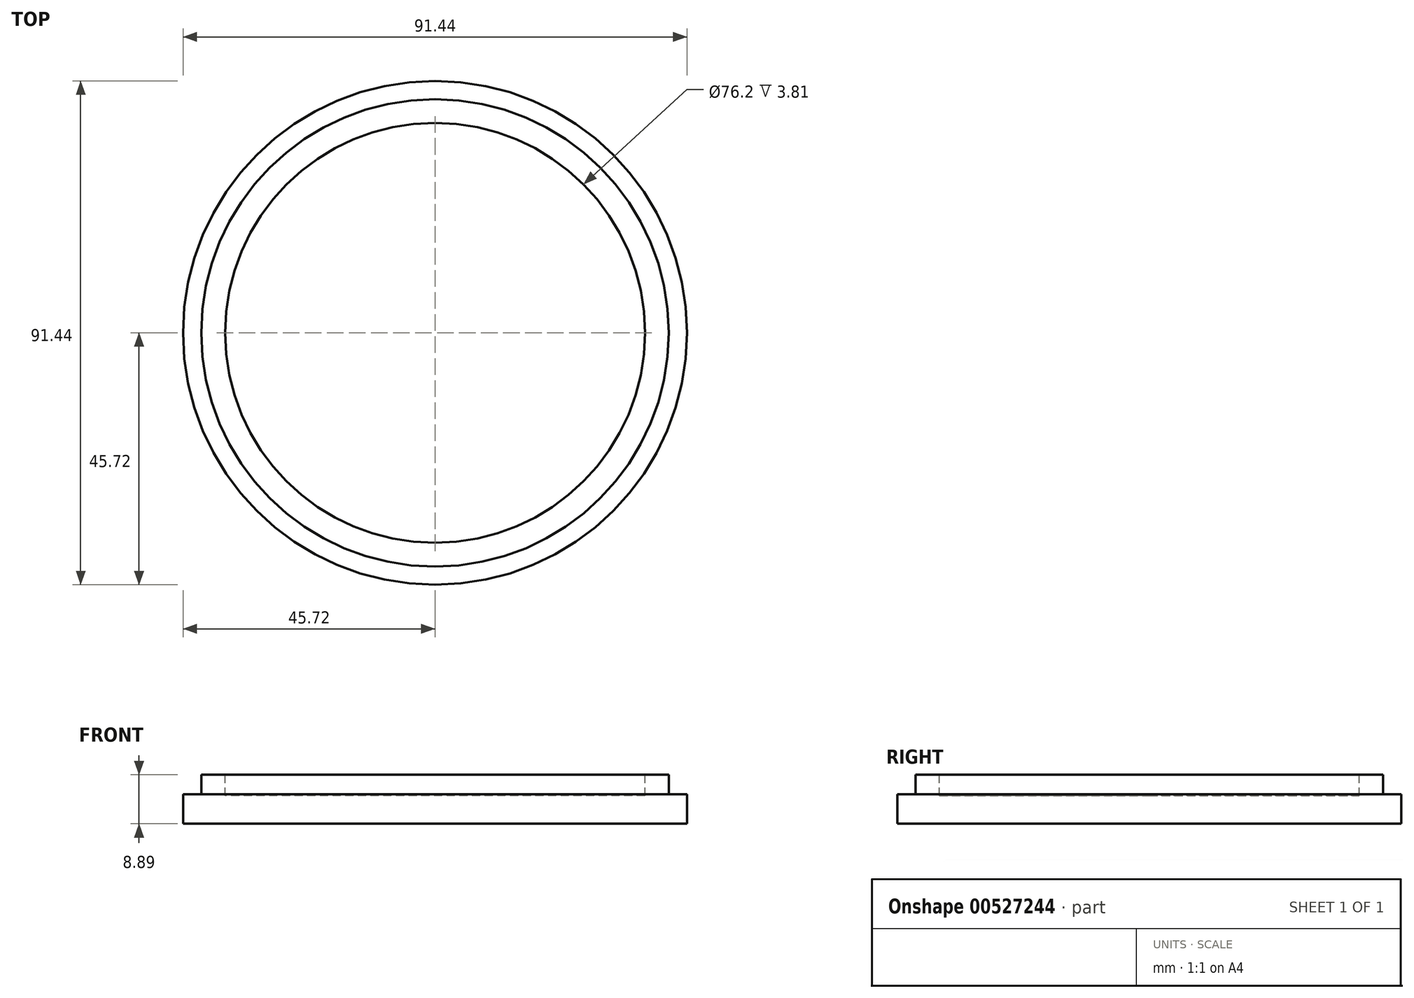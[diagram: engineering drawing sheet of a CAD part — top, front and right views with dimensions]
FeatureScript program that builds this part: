
annotation { "Feature Type Name" : "Feature", "Feature Type Description" : "" }
export const myFeature = defineFeature(function(context is Context, id is Id, definition is map)
    precondition{}
    {
        {
            var Q0;
            Q0=qCreatedBy(makeId("Top.planeOp"),FACE);
            var sketch = newSketch(context, id + "F0", { "sketchPlane" : qUnion([Q0])});
            skCircle(sketch, "E0", {"center": v(0, 0) * mm, "radius": 45.72 * mm});
            skSolve(sketch);
        }
        {
            var Q0;
            Q0 = qSketchRegion(id + "F0", true);
            extrude(context, id + "F1", {"entities" : qUnion([Q0]), "depth" : 5.33 * mm, "offsetDistance" : 25.4 * mm});
        }
        {
            var Q0;
            Q0=qCreatedBy(makeId("Top.planeOp"),FACE);
            var sketch = newSketch(context, id + "F2", { "sketchPlane" : qUnion([Q0])});
            skCircle(sketch, "E1", {"center": v(0, 0) * mm, "radius": 42.42 * mm});
            skSolve(sketch);
        }
        {
            var Q0;
            Q0 = qSketchRegion(id + "F2", true);
            extrude(context, id + "F3", {"entities" : qUnion([Q0]), "operationType" : NewBodyOperationType.ADD, "depth" : 8.9 * mm, "offsetDistance" : 25.4 * mm});
        }
        {
            var Q0;
            Q0=makeQuery(id+"F3.opExtrude","CAP_FACE",FACE,{"disambiguationData":[OSD([sQuery(id+"F2.wireOp",EDGE,"E1")])],"isStart":false});
            var sketch = newSketch(context, id + "F4", { "sketchPlane" : qUnion([Q0])});
            skCircle(sketch, "E2", {"center": v(0, 0) * mm, "radius": 38.1 * mm});
            skSolve(sketch);
        }
        {
            var Q0;
            Q0 = qSketchRegion(id + "F4", true);
            extrude(context, id + "F5", {"entities" : qUnion([Q0]), "operationType" : NewBodyOperationType.REMOVE, "depth" : -3.8 * mm, "offsetDistance" : 25.4 * mm});
        }
    });
